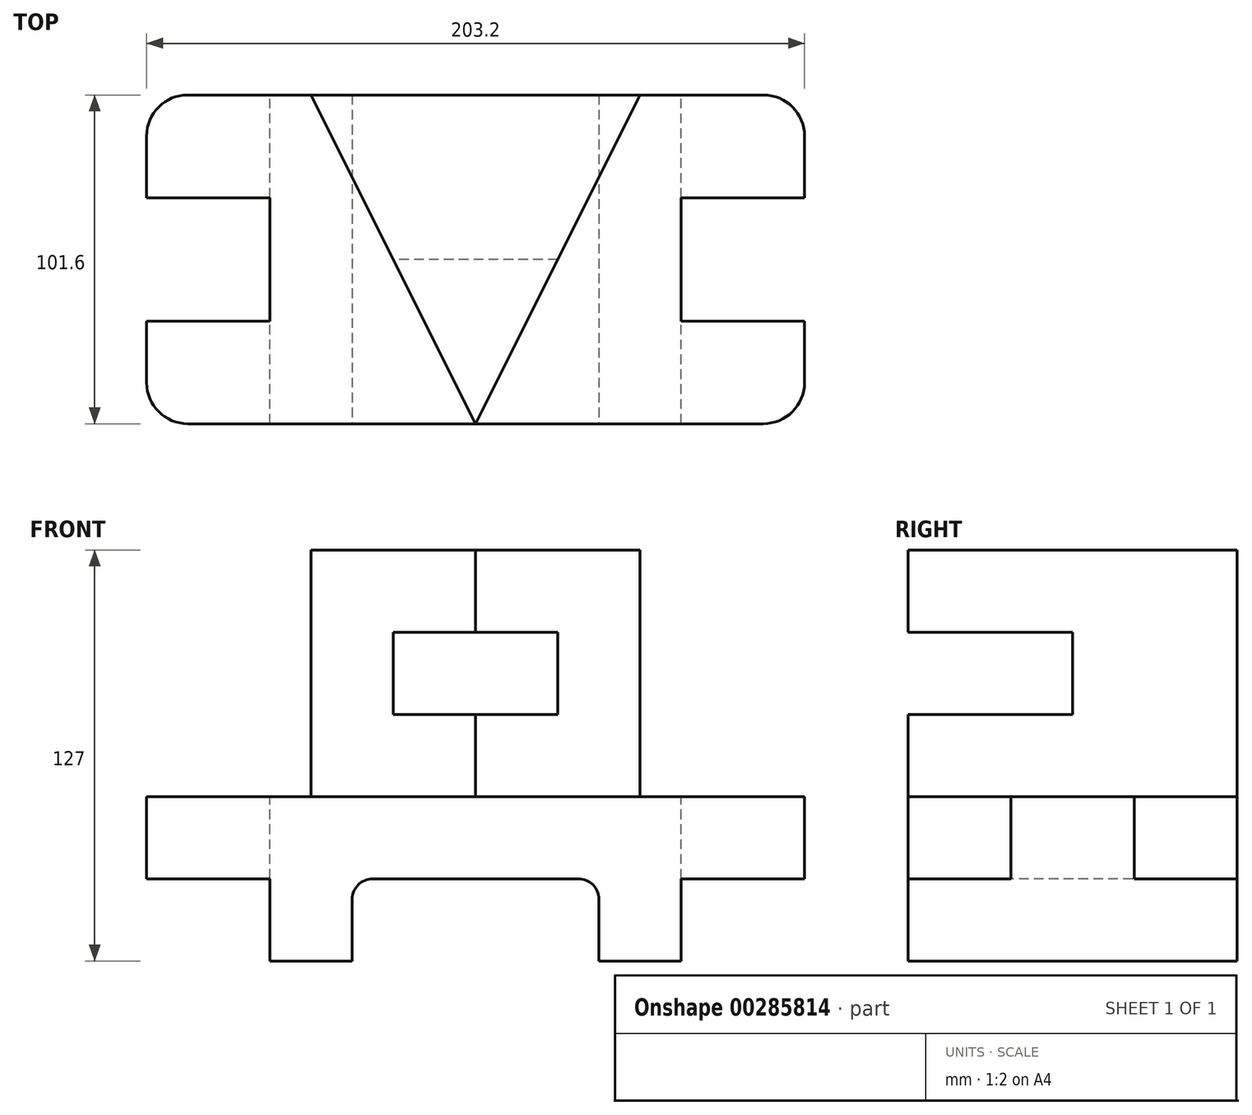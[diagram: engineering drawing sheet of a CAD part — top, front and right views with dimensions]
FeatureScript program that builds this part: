
annotation { "Feature Type Name" : "Feature", "Feature Type Description" : "" }
export const myFeature = defineFeature(function(context is Context, id is Id, definition is map)
    precondition{}
    {
        {
            var Q0;
            Q0=qCreatedBy(makeId("Front.planeOp"),FACE);
            var sketch = newSketch(context, id + "F0", { "sketchPlane" : qUnion([Q0])});
            skLineSegment(sketch, "E0.bottom", {"start": v(0, 0) * mm, "end": v(203.2, 0) * mm});
            skLineSegment(sketch, "E0.top", {"start": v(0, 50.8) * mm, "end": v(203.2, 50.8) * mm});
            skLineSegment(sketch, "E0.left", {"start": v(0, 0) * mm, "end": v(0, 50.8) * mm});
            skLineSegment(sketch, "E0.right", {"start": v(203.2, 0) * mm, "end": v(203.2, 50.8) * mm});
            skSolve(sketch);
        }
        {
            var Q0;
            Q0=makeQuery(id+"F0.imprint","IMPRINT",FACE,{"disambiguationData":[TD([[makeQuery(id+"F0.imprint","IMPRINT",EDGE,{"derivedFrom":sQuery(id+"F0.wireOp",EDGE,"E0.bottom")}),1.0]])]});
            extrude(context, id + "F1", {"entities" : qUnion([Q0]), "depth" : 101.6 * mm, "symmetric" : true});
        }
        {
            var Q0;
            Q0=makeQuery(id+"F1.opExtrude","SWEPT_FACE",FACE,{"disambiguationData":[OSD([sQuery(id+"F0.wireOp",EDGE,"E0.top")])]});
            var sketch = newSketch(context, id + "F2", { "sketchPlane" : qUnion([Q0])});
            skLineSegment(sketch, "E1", {"start": v(203.2, -19.05) * mm, "end": v(165.1, -19.05) * mm});
            skLineSegment(sketch, "E2", {"start": v(165.1, -19.05) * mm, "end": v(165.1, 19.05) * mm});
            skLineSegment(sketch, "E3", {"start": v(165.1, 19.05) * mm, "end": v(203.2, 19.05) * mm});
            skLineSegment(sketch, "E4", {"start": v(0, -19.05) * mm, "end": v(38.1, -19.05) * mm});
            skLineSegment(sketch, "E5", {"start": v(38.1, -19.05) * mm, "end": v(38.1, 19.05) * mm});
            skLineSegment(sketch, "E6", {"start": v(38.1, 19.05) * mm, "end": v(0, 19.05) * mm});
            skSolve(sketch);
        }
        {
            var Q0;
            {var subQ0=sQuery(id+"F2.wireOp",EDGE,"E1");Q0=makeQuery(id+"F2.imprint","IMPRINT",FACE,{"disambiguationData":[TD([[makeQuery(id+"F2.imprint","IMPRINT",EDGE,{"derivedFrom":subQ0}),-1.0]])]});}
            extrude(context, id + "F3", {"entities" : qUnion([Q0]), "operationType" : NewBodyOperationType.REMOVE, "endBound" : BoundingType.THROUGH_ALL, "oppositeDirection" : true, "depth" : 25.4 * mm});
        }
        {
            var Q0;
            {var subQ0=sQuery(id+"F2.wireOp",EDGE,"E4");Q0=makeQuery(id+"F2.imprint","IMPRINT",FACE,{"disambiguationData":[TD([[makeQuery(id+"F2.imprint","IMPRINT",EDGE,{"derivedFrom":subQ0}),1.0]])]});}
            extrude(context, id + "F4", {"entities" : qUnion([Q0]), "operationType" : NewBodyOperationType.REMOVE, "endBound" : BoundingType.THROUGH_ALL, "oppositeDirection" : true, "depth" : 25.4 * mm});
        }
        {
            var Q0;
            Q0=qCreatedBy(makeId("Right.planeOp"),FACE);
            var sketch = newSketch(context, id + "F5", { "sketchPlane" : qUnion([Q0])});
            skLineSegment(sketch, "E7", {"start": v(-50.8, 25.4) * mm, "end": v(50.8, 25.4) * mm});
            skLineSegment(sketch, "E8", {"start": v(-50.8, 25.4) * mm, "end": v(-50.8, 0) * mm});
            skLineSegment(sketch, "E9", {"start": v(-50.8, 0) * mm, "end": v(50.8, 0) * mm});
            skLineSegment(sketch, "E10", {"start": v(50.8, 0) * mm, "end": v(50.8, 25.4) * mm});
            skSolve(sketch);
        }
        {
            var Q0;
            Q0=makeQuery(id+"F5.imprint","IMPRINT",FACE,{"disambiguationData":[TD([[makeQuery(id+"F5.imprint","IMPRINT",EDGE,{"derivedFrom":sQuery(id+"F5.wireOp",EDGE,"E7")}),-1.0]])]});
            extrude(context, id + "F6", {"entities" : qUnion([Q0]), "operationType" : NewBodyOperationType.REMOVE, "depth" : 38.1 * mm});
        }
        {
            var Q0;
            Q0=makeQuery(id+"F3.boolean.opBoolean","COPY",FACE,{"derivedFrom":makeQuery(id+"F3.opExtrude","SWEPT_FACE",FACE,{"disambiguationData":[OSD([sQuery(id+"F2.wireOp",EDGE,"E2")])]})});
            var sketch = newSketch(context, id + "F7", { "sketchPlane" : qUnion([Q0])});
            skLineSegment(sketch, "E11", {"start": v(50.83, 0) * mm, "end": v(-50.8, 0) * mm});
            skPoint(sketch, "E11.endSnap0", {"position": v(0, 0) * mm});
            skLineSegment(sketch, "E12", {"start": v(-50.8, 0) * mm, "end": v(-50.8, 25.4) * mm});
            skLineSegment(sketch, "E13", {"start": v(-50.8, 25.4) * mm, "end": v(50.8, 25.4) * mm});
            skPoint(sketch, "E13.endSnap0", {"position": v(19.05, 25.4) * mm});
            skLineSegment(sketch, "E14", {"start": v(50.8, 25.4) * mm, "end": v(50.8, 0) * mm});
            skSolve(sketch);
        }
        {
            var Q0;
            {var subQ3=sQuery(id+"F7.wireOp",EDGE,"E14");Q0=makeQuery(id+"F7.imprint","IMPRINT",FACE,{"disambiguationData":[TD([[makeQuery(id+"F7.imprint","IMPRINT",EDGE,{"derivedFrom":subQ3}),-1.0]])]});}
            var Q1;
            {var subQ0=sQuery(id+"F7.wireOp",EDGE,"E11");var subQ1=sQuery(id+"F2.wireOp",EDGE,"E2");var subQ2=makeQuery(id+"F3.boolean.opBoolean","COPY",EDGE,{"derivedFrom":makeQuery(id+"F3.opExtrude","SWEPT_EDGE",EDGE,{"disambiguationData":[OSD([sQuery(id+"F2.wireOp",EDGE,"E1"),subQ1])]})});var subQ3=makeQuery(id+"F7.imprint","INTERSECT",VERTEX,{"derivedFrom":[subQ2,subQ0]});var subQ4=makeQuery(id+"F3.boolean.opBoolean","COPY",EDGE,{"derivedFrom":makeQuery(id+"F3.opExtrude","SWEPT_EDGE",EDGE,{"disambiguationData":[OSD([subQ1,sQuery(id+"F2.wireOp",EDGE,"E3")])]})});var subQ5=makeQuery(id+"F7.imprint","INTERSECT",VERTEX,{"derivedFrom":[subQ4,subQ0]});Q1=makeQuery(id+"F7.imprint","IMPRINT",FACE,{"disambiguationData":[TD([[makeQuery(id+"F7.imprint","IMPRINT",EDGE,{"disambiguationData":[TD([[subQ3,-1.0],[subQ5,1.0]])],"derivedFrom":subQ0}),1.0]])]});}
            var Q2;
            {var subQ3=sQuery(id+"F7.wireOp",EDGE,"E12");Q2=makeQuery(id+"F7.imprint","IMPRINT",FACE,{"disambiguationData":[TD([[makeQuery(id+"F7.imprint","IMPRINT",EDGE,{"derivedFrom":subQ3}),-1.0]])]});}
            extrude(context, id + "F8", {"entities" : qUnion([Q0, Q1, Q2]), "operationType" : NewBodyOperationType.REMOVE, "depth" : 38.1 * mm});
        }
        {
            var Q0;
            Q0=makeQuery(id+"F1.opExtrude","CAP_FACE",FACE,{"disambiguationData":[OSD([sQuery(id+"F0.wireOp",EDGE,"E0.bottom"),sQuery(id+"F0.wireOp",EDGE,"E0.top"),sQuery(id+"F0.wireOp",EDGE,"E0.left"),sQuery(id+"F0.wireOp",EDGE,"E0.right")])],"isStart":false});
            var sketch = newSketch(context, id + "F9", { "sketchPlane" : qUnion([Q0])});
            skLineSegment(sketch, "E15", {"start": v(63.5, 0) * mm, "end": v(63.5, 25.4) * mm});
            skLineSegment(sketch, "E16", {"start": v(63.5, 25.4) * mm, "end": v(139.7, 25.4) * mm});
            skLineSegment(sketch, "E17", {"start": v(139.7, 25.4) * mm, "end": v(139.7, 0) * mm});
            skArc(sketch, "E18", {"start": v(69.85, 25.4) * mm, "mid": v(65.36, 23.54) * mm, "end": v(63.5, 19.05) * mm});
            skArc(sketch, "E19", {"start": v(139.7, 19.05) * mm, "mid": v(137.84, 23.54) * mm, "end": v(133.35, 25.4) * mm});
            skSolve(sketch);
        }
        {
            var Q0;
            {var subQ0=sQuery(id+"F9.wireOp",EDGE,"E18");Q0=makeQuery(id+"F9.imprint","IMPRINT",FACE,{"disambiguationData":[TD([[makeQuery(id+"F9.imprint","IMPRINT",EDGE,{"derivedFrom":subQ0}),1.0]])]});}
            extrude(context, id + "F10", {"entities" : qUnion([Q0]), "operationType" : NewBodyOperationType.REMOVE, "endBound" : BoundingType.THROUGH_ALL, "oppositeDirection" : true, "depth" : 25.4 * mm});
        }
        {
            var Q0;
            {var subQ6=sQuery(id+"F2.wireOp",EDGE,"E1");Q0=makeQuery(id+"F2.imprint","IMPRINT",FACE,{"disambiguationData":[TD([[makeQuery(id+"F2.imprint","IMPRINT",EDGE,{"derivedFrom":subQ6}),1.0]])]});}
            var sketch = newSketch(context, id + "F11", { "sketchPlane" : qUnion([Q0])});
            skArc(sketch, "E20", {"start": v(190.5, -50.8) * mm, "mid": v(199.48, -47.08) * mm, "end": v(203.2, -38.1) * mm});
            skArc(sketch, "E21", {"start": v(203.2, 38.1) * mm, "mid": v(199.48, 47.08) * mm, "end": v(190.5, 50.8) * mm});
            skArc(sketch, "E22", {"start": v(12.7, 50.8) * mm, "mid": v(3.72, 47.08) * mm, "end": v(0, 38.1) * mm});
            skArc(sketch, "E23", {"start": v(0, -38.1) * mm, "mid": v(3.72, -47.08) * mm, "end": v(12.7, -50.8) * mm});
            skSolve(sketch);
        }
        {
            var Q0;
            {var subQ0=sQuery(id+"F11.wireOp",EDGE,"E22");Q0=makeQuery(id+"F11.imprint","IMPRINT",FACE,{"disambiguationData":[TD([[makeQuery(id+"F11.imprint","IMPRINT",EDGE,{"derivedFrom":subQ0}),-1.0]])]});}
            var Q1;
            {var subQ0=sQuery(id+"F11.wireOp",EDGE,"E23");Q1=makeQuery(id+"F11.imprint","IMPRINT",FACE,{"disambiguationData":[TD([[makeQuery(id+"F11.imprint","IMPRINT",EDGE,{"derivedFrom":subQ0}),-1.0]])]});}
            var Q2;
            {var subQ0=sQuery(id+"F11.wireOp",EDGE,"E20");Q2=makeQuery(id+"F11.imprint","IMPRINT",FACE,{"disambiguationData":[TD([[makeQuery(id+"F11.imprint","IMPRINT",EDGE,{"derivedFrom":subQ0}),-1.0]])]});}
            var Q3;
            {var subQ0=sQuery(id+"F11.wireOp",EDGE,"E21");Q3=makeQuery(id+"F11.imprint","IMPRINT",FACE,{"disambiguationData":[TD([[makeQuery(id+"F11.imprint","IMPRINT",EDGE,{"derivedFrom":subQ0}),-1.0]])]});}
            extrude(context, id + "F12", {"entities" : qUnion([Q0, Q1, Q2, Q3]), "operationType" : NewBodyOperationType.REMOVE, "endBound" : BoundingType.THROUGH_ALL, "oppositeDirection" : true, "depth" : 25.4 * mm});
        }
        {
            var Q0;
            {var subQ6=sQuery(id+"F2.wireOp",EDGE,"E1");Q0=makeQuery(id+"F2.imprint","IMPRINT",FACE,{"disambiguationData":[TD([[makeQuery(id+"F2.imprint","IMPRINT",EDGE,{"derivedFrom":subQ6}),1.0]])]});}
            var sketch = newSketch(context, id + "F13", { "sketchPlane" : qUnion([Q0])});
            skLineSegment(sketch, "E24", {"start": v(50.8, 50.8) * mm, "end": v(152.4, 50.8) * mm});
            skLineSegment(sketch, "E25", {"start": v(50.8, 50.8) * mm, "end": v(101.6, -50.8) * mm});
            skLineSegment(sketch, "E26", {"start": v(152.4, 50.8) * mm, "end": v(101.6, -50.8) * mm});
            skSolve(sketch);
        }
        {
            var Q0;
            Q0=makeQuery(id+"F13.imprint","IMPRINT",FACE,{"disambiguationData":[TD([[makeQuery(id+"F13.imprint","IMPRINT",EDGE,{"derivedFrom":sQuery(id+"F13.wireOp",EDGE,"E24")}),-1.0]])]});
            extrude(context, id + "F14", {"entities" : qUnion([Q0]), "operationType" : NewBodyOperationType.ADD, "depth" : 76.2 * mm});
        }
        {
            var Q0;
            Q0=makeQuery(id+"F14.opExtrude","CAP_FACE",FACE,{"disambiguationData":[OSD([sQuery(id+"F13.wireOp",EDGE,"E24"),sQuery(id+"F13.wireOp",EDGE,"E25"),sQuery(id+"F13.wireOp",EDGE,"E26")])],"isStart":false});
            var sketch = newSketch(context, id + "F15", { "sketchPlane" : qUnion([Q0])});
            skLineSegment(sketch, "E27", {"start": v(127, 0) * mm, "end": v(76.2, 0) * mm});
            skSolve(sketch);
        }
        {
            var Q0;
            {var subQ0=sQuery(id+"F15.wireOp",EDGE,"E27");Q0=makeQuery(id+"F15.imprint","IMPRINT",FACE,{"disambiguationData":[TD([[makeQuery(id+"F15.imprint","IMPRINT",EDGE,{"derivedFrom":subQ0}),1.0]])]});}
            extrude(context, id + "F16", {"entities" : qUnion([Q0]), "operationType" : NewBodyOperationType.REMOVE, "oppositeDirection" : true, "depth" : 50.8 * mm, "hasSecondDirection" : true, "secondDirectionOppositeDirection" : true, "secondDirectionDepth" : 25.4 * mm});
        }
    });
